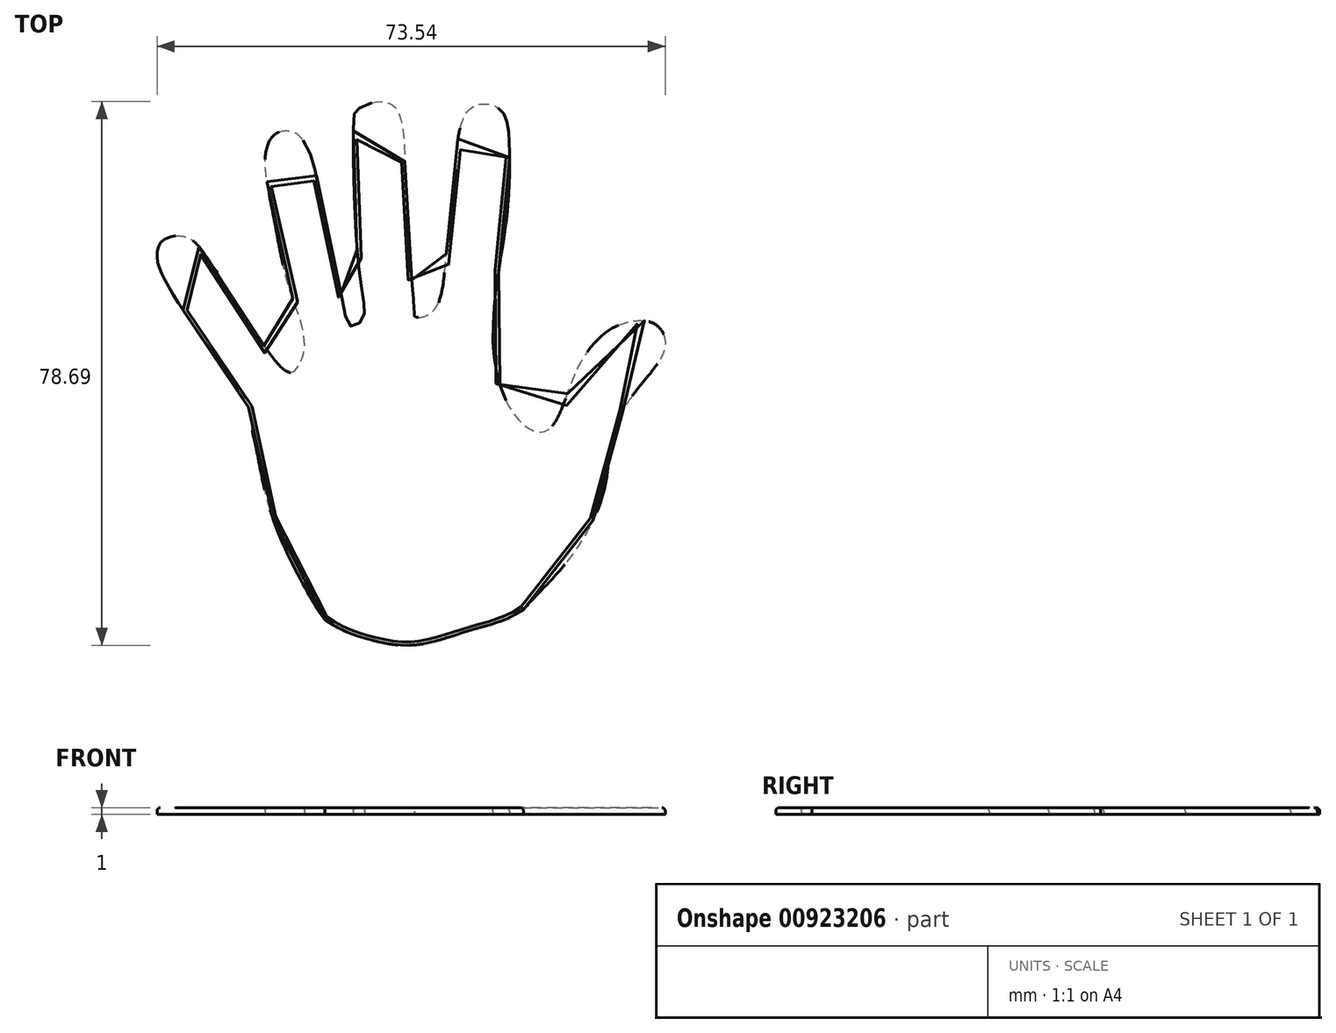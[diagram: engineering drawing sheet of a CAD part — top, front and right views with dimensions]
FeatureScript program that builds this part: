
annotation { "Feature Type Name" : "Feature", "Feature Type Description" : "" }
export const myFeature = defineFeature(function(context is Context, id is Id, definition is map)
    precondition{}
    {
        {
            var Q0;
            Q0=qCreatedBy(makeId("Top.planeOp"),FACE);
            var sketch = newSketch(context, id + "F0", { "sketchPlane" : qUnion([Q0])});
            skLineSegment(sketch, "E0", {"start": v(0, 0) * mm, "end": v(0, 90) * mm, "construction": true});
            skFitSpline(sketch, "E1", {"points": [v(-7.62, 10.08) * mm, v(-11.32, 16.32) * mm, v(-15.53, 26.02) * mm, v(-17.64, 35.41) * mm, v(-18.1, 37.59) * mm, v(-18.6, 40.73) * mm, v(-22.65, 47.04) * mm, v(-30.09, 58.05) * mm, v(-31.85, 62.41) * mm, v(-31.04, 64.98) * mm, v(-27.66, 65.47) * mm, v(-25.4, 63.54) * mm, v(-21.35, 57.4) * mm, v(-13.25, 46.09) * mm, v(-11.83, 46.25) * mm, v(-10.53, 49.95) * mm, v(-12.78, 58.2) * mm, v(-15.05, 68.55) * mm, v(-16.17, 77.45) * mm, v(-14.55, 80.5) * mm, v(-11.82, 80.5) * mm, v(-9.4, 76.64) * mm, v(-8.26, 70.8) * mm, v(-7.12, 64.35) * mm, v(-5.16, 56.97) * mm, v(-3.87, 52.56) * mm, v(-2.23, 53.38) * mm, v(-1.85, 55.3) * mm, v(-2.75, 61.6) * mm, v(-3.4, 82.64) * mm, v(-2.91, 83.9) * mm, v(0, 85.04) * mm, v(2.56, 84.23) * mm, v(3.74, 80.69) * mm, v(4.09, 73.2) * mm, v(4.89, 60.28) * mm, v(5.34, 54.6) * mm, v(5.53, 53.9) * mm, v(8.12, 54.8) * mm, v(10.01, 63.38) * mm, v(11, 69.53) * mm, v(11.47, 77.44) * mm, v(12.11, 81.65) * mm, v(14.05, 84.43) * mm, v(17.8, 83.93) * mm, v(19.08, 79.22) * mm, v(19.08, 72.76) * mm, v(18.32, 65.32) * mm, v(16.8, 49.47) * mm, v(20.51, 38.96) * mm, v(24.59, 37.48) * mm, v(28.61, 45.6) * mm, v(34.27, 52.4) * mm, v(40.1, 52.9) * mm, v(41.57, 49.3) * mm, v(36.7, 42.2) * mm, v(33.79, 34.92) * mm, v(32.5, 27.64) * mm, v(27.16, 18.1) * mm, v(21.15, 11.57) * mm], "startDerivative": vector(-208.02, 285.5) * mm, "endDerivative": vector(-281.48, -321.48) * mm});
            skFitSpline(sketch, "E2", {"points": [v(-7.62, 10.08) * mm, v(-1.76, 7.38) * mm, v(5.36, 6.41) * mm, v(12.86, 8.36) * mm, v(18.45, 10.08) * mm, v(21.15, 11.57) * mm], "startDerivative": vector(26.3, -18.59) * mm, "endDerivative": vector(15.02, 10.01) * mm});
            skSolve(sketch);
        }
        {
            var Q0;
            Q0=makeQuery(id+"F0.imprint","IMPRINT",FACE,{"disambiguationData":[TD([[makeQuery(id+"F0.imprint","IMPRINT",EDGE,{"derivedFrom":sQuery(id+"F0.wireOp",EDGE,"E1")}),-1.0]])]});
            extrude(context, id + "F1", {"entities" : qUnion([Q0]), "depth" : 1 * mm, "offsetDistance" : 25 * mm});
        }
        {
            var Q0;
            Q0=makeQuery(id+"F1.opExtrude","CAP_EDGE",EDGE,{"disambiguationData":[OSD([sQuery(id+"F0.wireOp",EDGE,"E1")])],"isStart":false});
            var Q1;
            Q1=makeQuery(id+"F1.opExtrude","CAP_EDGE",EDGE,{"disambiguationData":[OSD([sQuery(id+"F0.wireOp",EDGE,"E2")])],"isStart":false});
            fillet(context, id + "F2", {"entities" : qUnion([Q0, Q1]), "radius" : 0.5 * mm, "tangentPropagation" : true, "allowEdgeOverflow" : false});
        }
    });
